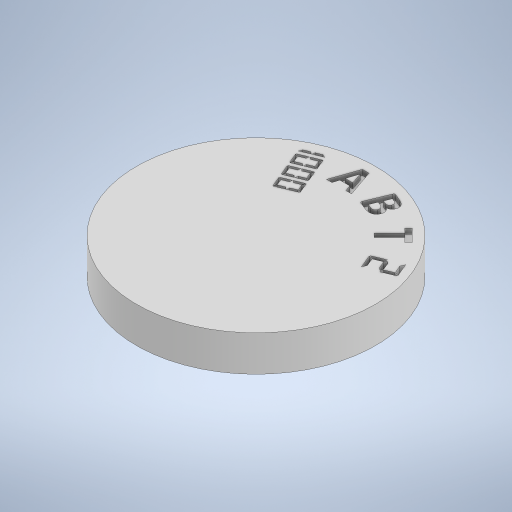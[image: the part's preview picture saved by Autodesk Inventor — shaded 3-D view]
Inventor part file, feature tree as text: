
AUTODESK INVENTOR PART (.ipt)
format: ipt  version: 2023 (Build 270158000, 158)  size: 404,480 bytes
history: native  units: mm
features: extrude x3, sketch x3
ambient origin geometry x8: Origin, YZ Plane, XZ Plane, XY Plane, X Axis, Y Axis, Z Axis, Center Point
bodies: 实体1 (feature_tree)
feature tree (6):
  extrude  "拉伸1"  Depth=2.1mm
  extrude  "拉伸2"  Depth=2.3mm TaperAngle=0.0deg
  extrude  "拉伸3"  Depth=0.4mm
  sketch  "草图1"  dims[d0=3.0mm d1=2.1mm]
  sketch  "草图2"  dims[d2=18.0mm d3=2.3mm d4=0.0mm]
  sketch  "草图3"  dims[d5=0.4mm d6=0.0mm d7=18.0mm d12=0.4mm d13=0.0mm d15=160.0mm d17=360.0deg d19=6.3mm d20=6.3mm d21=6.3mm d22=6.3mm d23=5.0mm]
